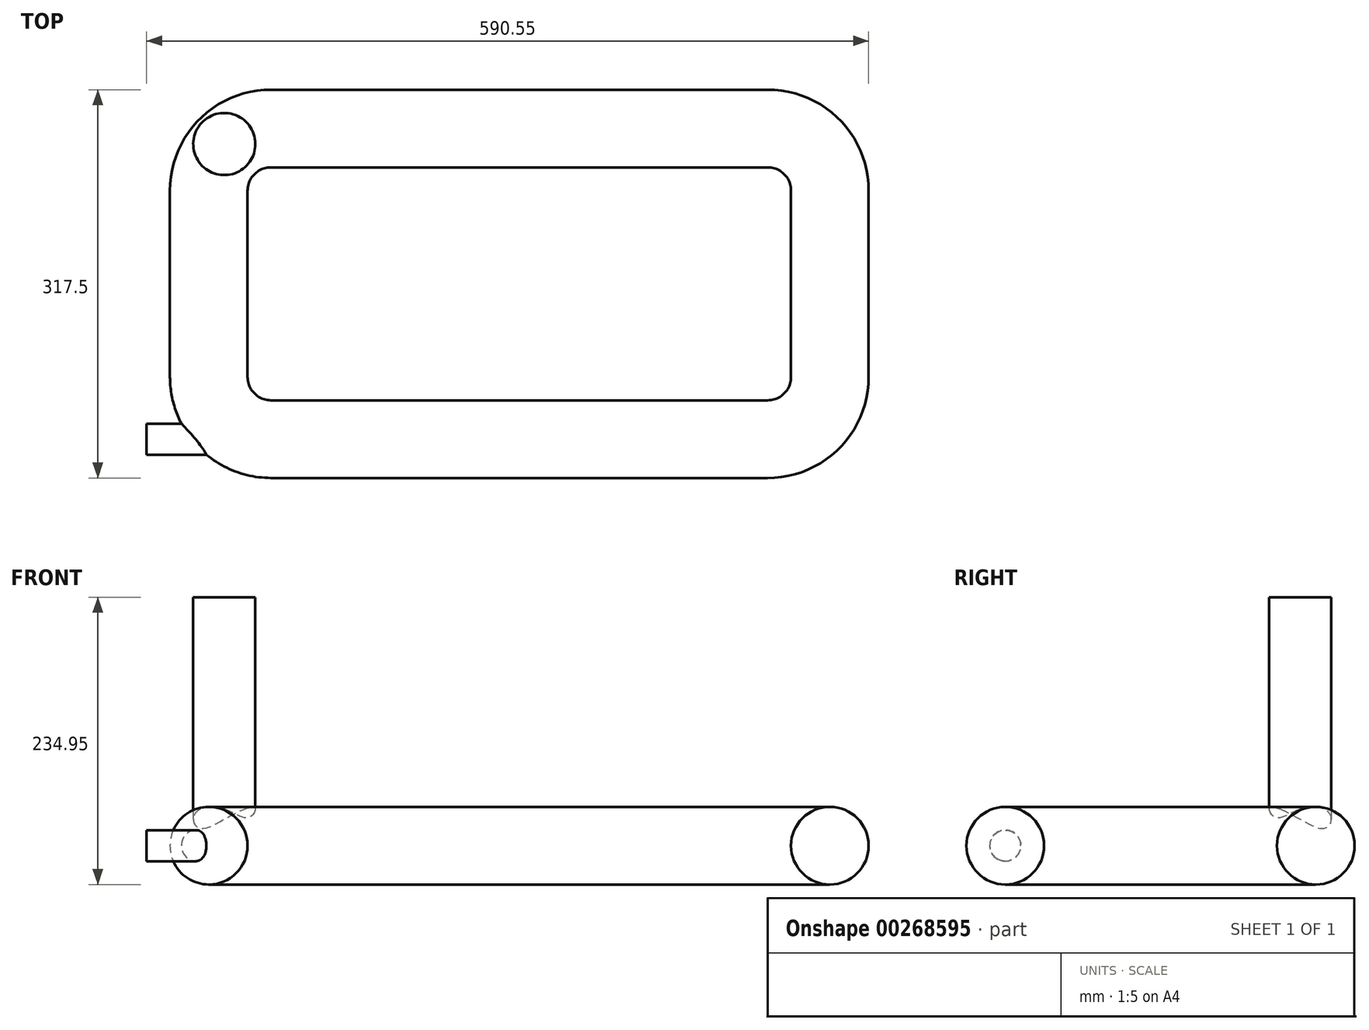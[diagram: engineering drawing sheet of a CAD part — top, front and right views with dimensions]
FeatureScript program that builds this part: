
annotation { "Feature Type Name" : "Feature", "Feature Type Description" : "" }
export const myFeature = defineFeature(function(context is Context, id is Id, definition is map)
    precondition{}
    {
        {
            var Q0;
            Q0=qCreatedBy(makeId("Front.planeOp"),FACE);
            var sketch = newSketch(context, id + "F0", { "sketchPlane" : qUnion([Q0])});
            skCircle(sketch, "E0", {"center": v(-254, 0) * mm, "radius": 31.75 * mm});
            skSolve(sketch);
        }
        {
            var Q0;
            Q0=qCreatedBy(makeId("Top.planeOp"),FACE);
            var sketch = newSketch(context, id + "F1", { "sketchPlane" : qUnion([Q0])});
            skLineSegment(sketch, "E1", {"start": v(-203.2, 127) * mm, "end": v(203.2, 127) * mm});
            skLineSegment(sketch, "E2", {"start": v(254, 76.2) * mm, "end": v(254, -76.2) * mm});
            skLineSegment(sketch, "E3", {"start": v(203.2, -127) * mm, "end": v(-203.2, -127) * mm});
            skLineSegment(sketch, "E4", {"start": v(-254, -76.2) * mm, "end": v(-254, 76.2) * mm});
            skPoint(sketch, "E5.visualSharp", {"position": v(-254, -127) * mm});
            skArc(sketch, "E5.filletArc", {"start": v(-254, -76.2) * mm, "mid": v(-239.12, -112.12) * mm, "end": v(-203.2, -127) * mm});
            skPoint(sketch, "E6.visualSharp", {"position": v(-254, 127) * mm});
            skArc(sketch, "E6.filletArc", {"start": v(-203.2, 127) * mm, "mid": v(-239.12, 112.12) * mm, "end": v(-254, 76.2) * mm});
            skPoint(sketch, "E7.visualSharp", {"position": v(254, 127) * mm});
            skArc(sketch, "E7.filletArc", {"start": v(254, 76.2) * mm, "mid": v(239.12, 112.12) * mm, "end": v(203.2, 127) * mm});
            skPoint(sketch, "E8.visualSharp", {"position": v(254, -127) * mm});
            skArc(sketch, "E8.filletArc", {"start": v(203.2, -127) * mm, "mid": v(239.12, -112.12) * mm, "end": v(254, -76.2) * mm});
            skSolve(sketch);
        }
        {
            var Q0;
            Q0=makeQuery(id+"F0.imprint","IMPRINT",FACE,{"disambiguationData":[TD([[makeQuery(id+"F0.imprint","IMPRINT",EDGE,{"derivedFrom":sQuery(id+"F0.wireOp",EDGE,"E0")}),1.0]])]});
            var Q1;
            Q1=sQuery(id+"F1.wireOp",EDGE,"E6.filletArc");
            var Q2;
            Q2=sQuery(id+"F1.wireOp",EDGE,"E4");
            var Q3;
            Q3=sQuery(id+"F1.wireOp",EDGE,"E3");
            var Q4;
            Q4=sQuery(id+"F1.wireOp",EDGE,"E8.filletArc");
            var Q5;
            Q5=sQuery(id+"F1.wireOp",EDGE,"E2");
            var Q6;
            Q6=sQuery(id+"F1.wireOp",EDGE,"E7.filletArc");
            var Q7;
            Q7=sQuery(id+"F1.wireOp",EDGE,"E1");
            var Q8;
            Q8=sQuery(id+"F1.wireOp",EDGE,"E5.filletArc");
            sweep(context, id + "F2", {"profiles" : qUnion([Q0]), "path" : qUnion([Q1, Q2, Q3, Q4, Q5, Q6, Q7, Q8])});
        }
        {
            var Q0;
            Q0=qCreatedBy(makeId("Right.planeOp"),FACE);
            var sketch = newSketch(context, id + "F3", { "sketchPlane" : qUnion([Q0])});
            skCircle(sketch, "E9", {"center": v(-127, 0) * mm, "radius": 12.7 * mm});
            skSolve(sketch);
        }
        {
            var Q0;
            Q0 = qSketchRegion(id + "F3", true);
            extrude(context, id + "F4", {"entities" : qUnion([Q0]), "operationType" : NewBodyOperationType.ADD, "oppositeDirection" : true, "depth" : 304.8 * mm, "offsetDistance" : 25.4 * mm});
        }
        {
            var Q0;
            Q0=qCreatedBy(makeId("Top.planeOp"),FACE);
            var sketch = newSketch(context, id + "F5", { "sketchPlane" : qUnion([Q0])});
            skCircle(sketch, "E10", {"center": v(-241.3, 114.3) * mm, "radius": 25.4 * mm});
            skSolve(sketch);
        }
        {
            var Q0;
            Q0 = qSketchRegion(id + "F5", true);
            extrude(context, id + "F6", {"entities" : qUnion([Q0]), "operationType" : NewBodyOperationType.ADD, "depth" : 203.2 * mm, "offsetDistance" : 25.4 * mm});
        }
    });
